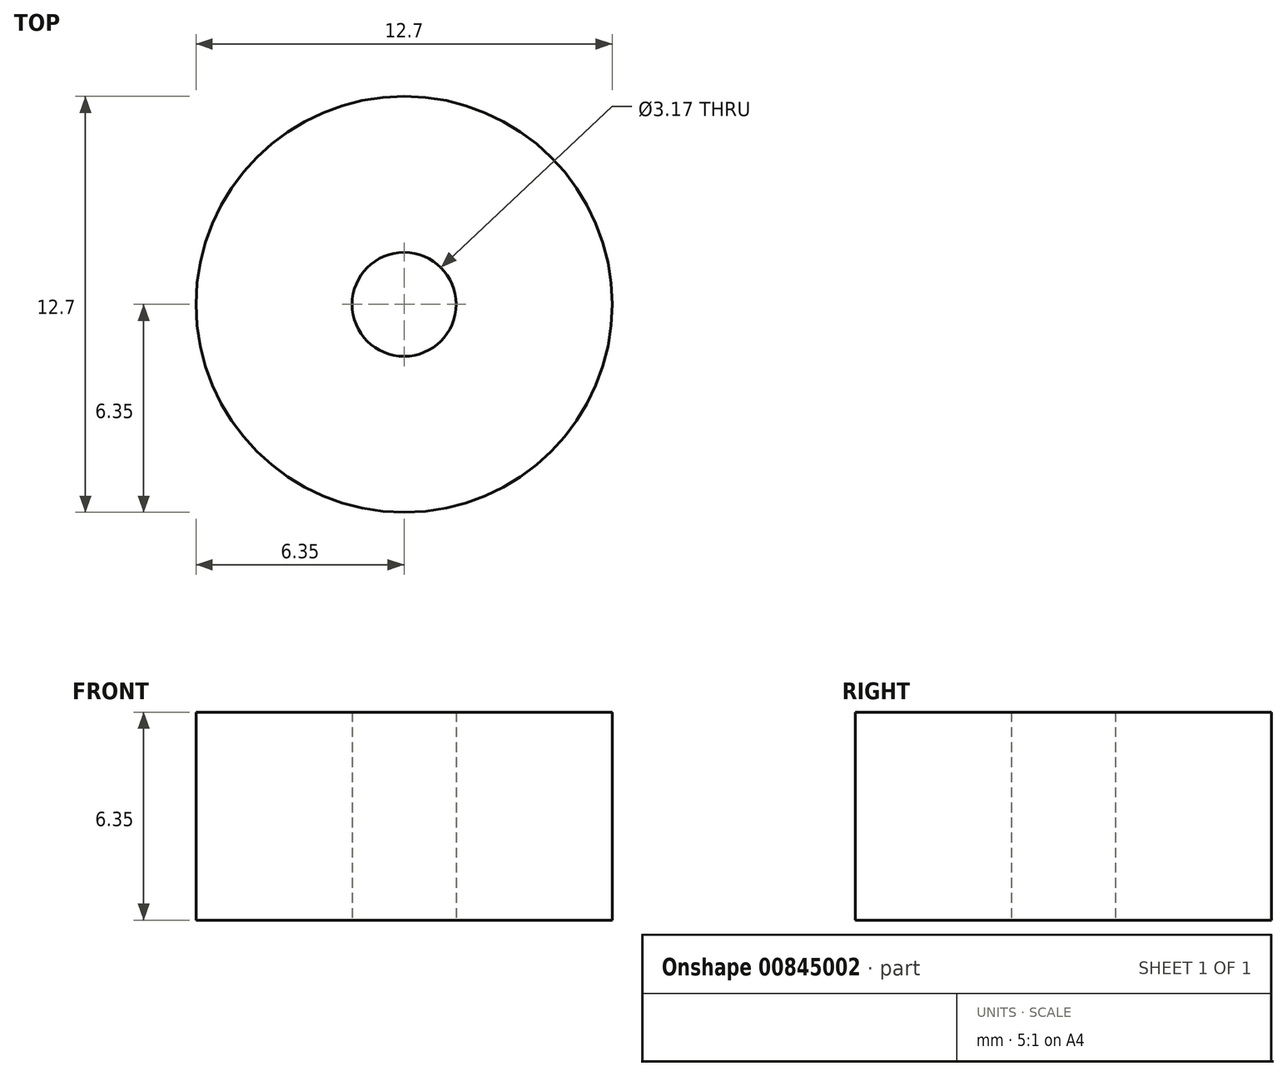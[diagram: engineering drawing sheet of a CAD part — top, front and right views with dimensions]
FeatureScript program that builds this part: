
annotation { "Feature Type Name" : "Feature", "Feature Type Description" : "" }
export const myFeature = defineFeature(function(context is Context, id is Id, definition is map)
    precondition{}
    {
        {
            var Q0;
            Q0=qCreatedBy(makeId("Top.planeOp"),FACE);
            var sketch = newSketch(context, id + "F0", { "sketchPlane" : qUnion([Q0])});
            skCircle(sketch, "E0", {"center": v(0, 0) * mm, "radius": 1.59 * mm});
            skCircle(sketch, "E1", {"center": v(0, 0) * mm, "radius": 6.35 * mm});
            skSolve(sketch);
        }
        {
            var Q0;
            Q0=makeQuery(id+"F0.imprint","IMPRINT",FACE,{"disambiguationData":[TD([[makeQuery(id+"F0.imprint","IMPRINT",EDGE,{"derivedFrom":sQuery(id+"F0.wireOp",EDGE,"E0")}),-1.0]])]});
            extrude(context, id + "F1", {"entities" : qUnion([Q0]), "depth" : 6.35 * mm, "offsetDistance" : 25.4 * mm});
        }
    });
